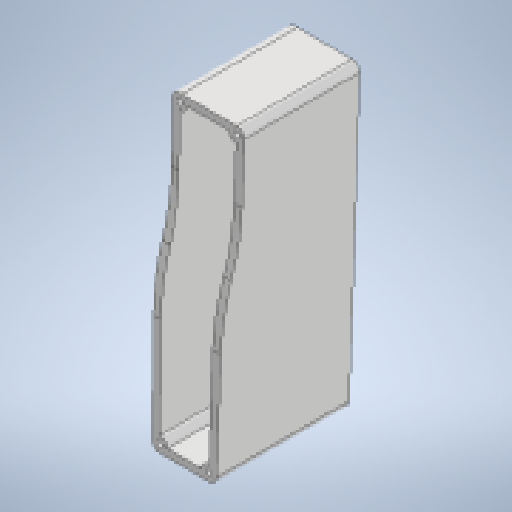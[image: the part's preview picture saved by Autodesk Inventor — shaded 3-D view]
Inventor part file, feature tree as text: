
AUTODESK INVENTOR PART (.ipt)
format: ipt  version: 2025.1 (Build 291241000, 241)  size: 231,424 bytes
history: native  units: mm
features: other x7, reference x4, sketch x3, extrude x3, fillet x2, projected_geometry x2
ambient origin geometry x8: Origin, YZ Plane, XZ Plane, XY Plane, X Axis, Y Axis, Z Axis, Center Point
bodies: Body1 (feature_tree)
feature tree (21):
  other  "ソリッド1"
  sketch  "スケッチ1"
  other  "作業平面1"
  extrude  "押し出し1"  Depth=1.6mm
  sketch  "スケッチ2"
  other  "作業平面2"
  extrude  "押し出し2"  Depth=1.6mm
  fillet  "フィレット1"  Radius=1.6mm
  extrude  "押し出し3"  Depth=1.6mm
  fillet  "フィレット2"  Radius=4.0mm
  reference  "参照1"
  reference  "参照2"
  reference  "参照3"
  reference  "参照4"
  projected_geometry  "投影ループ1"
  sketch  "スケッチ3"
  projected_geometry  "投影ループ2"
  other  "<userpath>\Documents\Inventor\Vixen\doutai.iam"
  other  "doutai.iam"
  other  "newnewude:1"
  other  "newnewude_2:1"
